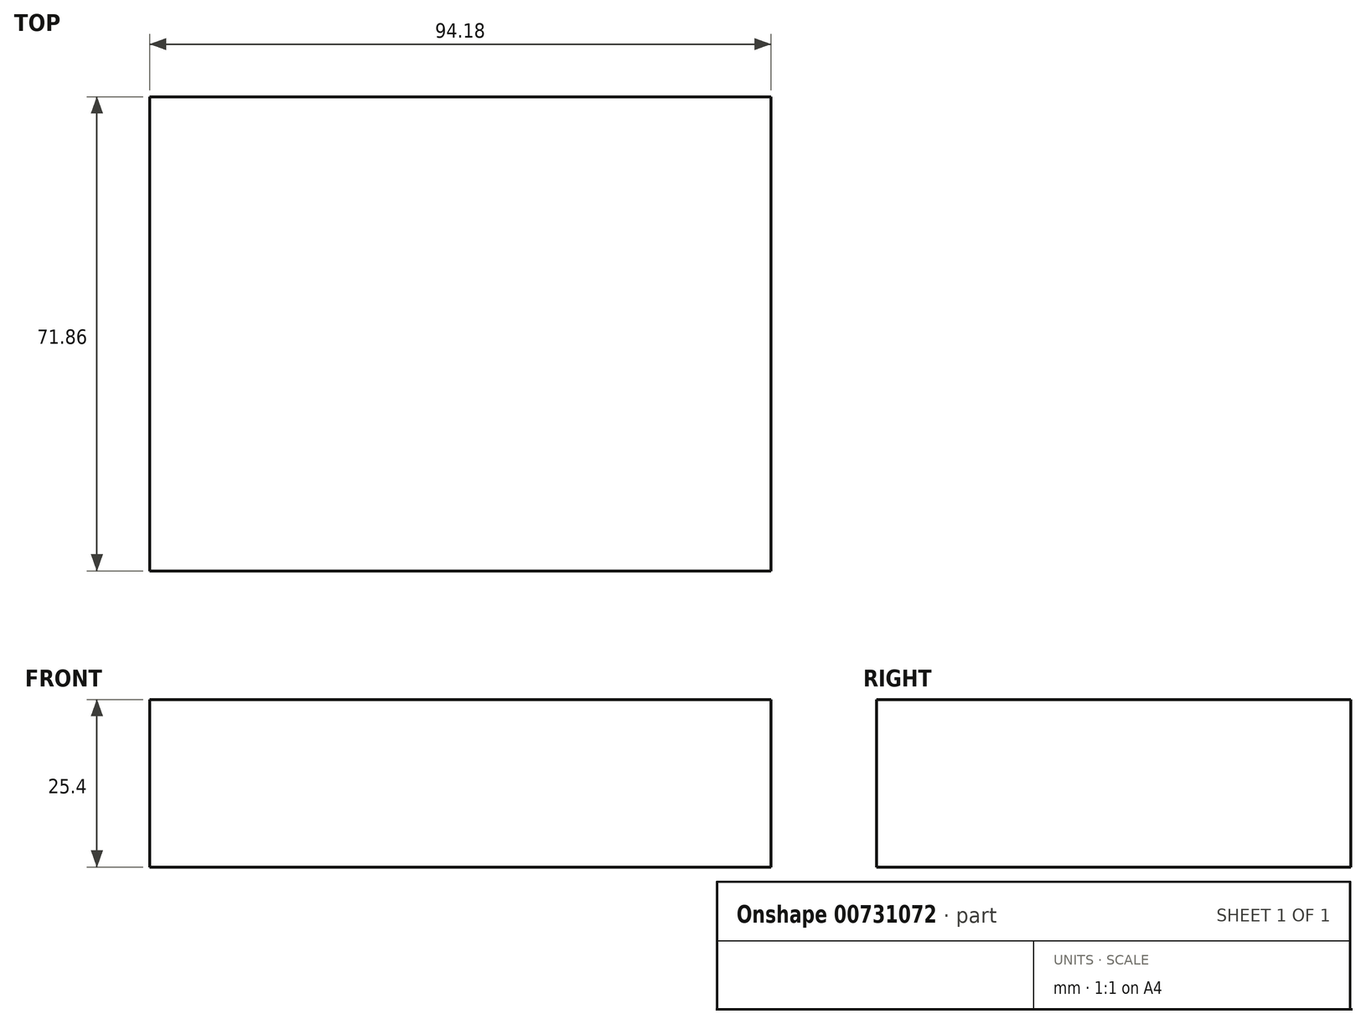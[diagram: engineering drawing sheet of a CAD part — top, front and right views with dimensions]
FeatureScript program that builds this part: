
annotation { "Feature Type Name" : "Feature", "Feature Type Description" : "" }
export const myFeature = defineFeature(function(context is Context, id is Id, definition is map)
    precondition{}
    {
        {
            var Q0;
            Q0=qCreatedBy(makeId("Top.planeOp"),FACE);
            var sketch = newSketch(context, id + "F0", { "sketchPlane" : qUnion([Q0])});
            skLineSegment(sketch, "E0.bottom", {"start": v(47.09, 35.93) * mm, "end": v(-47.09, 35.93) * mm});
            skLineSegment(sketch, "E0.top", {"start": v(47.09, -35.93) * mm, "end": v(-47.09, -35.93) * mm});
            skLineSegment(sketch, "E0.left", {"start": v(47.09, 35.93) * mm, "end": v(47.09, -35.93) * mm});
            skLineSegment(sketch, "E0.right", {"start": v(-47.09, 35.93) * mm, "end": v(-47.09, -35.93) * mm});
            skPoint(sketch, "E0.middle", {"position": v(0, 0) * mm});
            skSolve(sketch);
        }
        {
            var Q0;
            Q0 = qSketchRegion(id + "F0", true);
            extrude(context, id + "F1", {"entities" : qUnion([Q0]), "depth" : 25.4 * mm, "offsetDistance" : 25.4 * mm});
        }
    });
